# Revit family: Faucet-Lavatory-KALLISTA-One-P32412_1
name_source: partatom
category: Plumbing Fixtures
units: mm (PartAtom-declared; Revit-internal decimal feet)

## family parameters
Cut with Voids When Loaded = No
Host = Face
OmniClass Number = 23.31.11.00
OmniClass Title = Faucets
Part Type = Normal
Room Calculation Point = No
Round Connector Dimension = Use Diameter
Shared = No

## types (5) — shared parameters
ADA Compliant = No
Assembly Code = D2010
CW Connection = Yes
Cold Water Inlet = Cold Water Inlet
Date Modified = 05/22/2023
Default Elevation = 36"
Description = FP5 Sink Faucet Low Spout
Drain Included = No
Flow Rate = 2 GPM
HW Connection = Yes
Handle Clearance = 2 13/16"
Height = 3"
Hot Water Inlet = Hot Water Inlet
Length = 5 5/16"
Manufacturer = Kallista Co.
Master Format 2014 = 22 41 39
Master Format 2014 Name = Residential Faucets, Supplies, and Trim
Material = Premium Metal Construction
Pressure = 60.00 psi
Product Name = One
Spout Reach = 5 5/16"
URL = https://www.kallista.com
Vent Connection = No
Waste Connection = No
Waste Water Outlet = Waste Water Outlet
WaterSense Certified = No

## per-type parameters (varying)
| type | Finish | Model | Type |
| BAF-Brushed French Gold | Kallista-Metal-BAF-Brushed_French_Gold | P32412-LV-BAF | 1 |
| BL-Matte Black | Kallista-Metal-BL-Matte_Black | P32412-LV-BL | 2 |
| BN-Brushed Nickel | Kallista-Metal-BN-Brushed_Nickel | P32412-LV-BN | 3 |
| CP-Chrome | Kallista-Metal-CP-Chrome | P32412-LV-CP | 4 |
| SN-Polished Nickel | Kallista-Metal-SN-Polished_Nickel | P32412-LV-SN | 5 |

## geometry (parser evidence)
native form markers: Sweep x7
no freeform markers — native parametric forms only
